# Revit family: Specialty_Equipment-Bavis_Fabacraft-Premium_Drive-Up_Window NEW
name_source: partatom
category: Specialty Equipment
units: mm (PartAtom-declared; Revit-internal decimal feet)

## family parameters
Always vertical = Yes
Cut with Voids When Loaded = No
Host = Wall
OmniClass Number = 23.40.70.27.24.21
OmniClass Title = Service and Teller Window Units
Part Type = Normal
Room Calculation Point = No
Round Connector Dimension = Use Diameter
Shared = No

## types (10) — shared parameters
Assembly Code = B2020100
Default Elevation = 0' - 0"
Depth = 0' - 6 3/4"
Finish = Metal - Bavis Fabacraft -Aluminum
Glazing = Glass - Bavis Fabacraft - Clear
Height = 2' - 8 3/4"
Instruction Sheet Link = https://docs.bavis.com
Keynote = 08 51 00
Manufacturer = Bavis Fabacraft
Product Documentation Link = https://docs.bavis.com
Product Name = Bavis Premium Drive-Up Windows
Product Page URL = https://www.bavis.com
Rough Height = 2' - 9"
URL = https://www.bavis.com
Version = 2020 - v1.0a
Video Link = https://www.youtube.com

## per-type parameters (varying)
| type | 10L | 12L | C Center 1 | C Center 2 | Constraints | Model | Rough Width | Trim | Warranty URL | Width |
| 3' Series Window - Trimless | No | No | 0' - 0" | 0' - 0" | 3 | 12001015 | 2' - 8 1/2" | No |  | 2' - 8" |
| 5' Series Window - Trimless | No | No | 0' - 0" | 0' - 0" | 5 | 12001006 | 4' - 8 1/2" | No |  | 4' - 8" |
| 8' Series Window - Trimless | No | No | 0' - 0" | 0' - 0" | 8 | 12001007 | 7' - 4 7/8" | No |  | 7' - 4 3/8" |
| 10' Series Window - Trimless | Yes | No | 4' - 7 3/4" | 0' - 0" | 10 | 12001008 | 9' - 4" | No |  | 9' - 3 1/2" |
| 12' Series Window - Trimless | Yes | Yes | 3' - 10 11/256" | 3' - 10 11/256" | 12 | 12001002 | 11' - 6 5/8" | No |  | 11' - 6 1/8" |
| 3' Series Window - Trim | No | No | 0' - 0" | 0' - 0" | 3 | 12000987 | 2' - 8 1/2" | Yes | Contact Manufacturer for Warranty Information | 2' - 8" |
| 5' Series Window - Trim | No | No | 0' - 0" | 0' - 0" | 5 | 12000994 | 4' - 8 1/2" | Yes |  | 4' - 8" |
| 8' Series Window - Trim | No | No | 0' - 0" | 0' - 0" | 8 | 12000996 | 7' - 4 7/8" | Yes |  | 7' - 4 3/8" |
| 10' Series Window - Trim | Yes | No | 4' - 7 3/4" | 0' - 0" | 10 | 12000995 | 9' - 4" | Yes |  | 9' - 3 1/2" |
| 12' Series Window - Trim | Yes | Yes | 3' - 10 11/256" | 3' - 10 11/256" | 12 | 12001000 | 11' - 6 5/8" | Yes |  | 11' - 6 1/8" |
